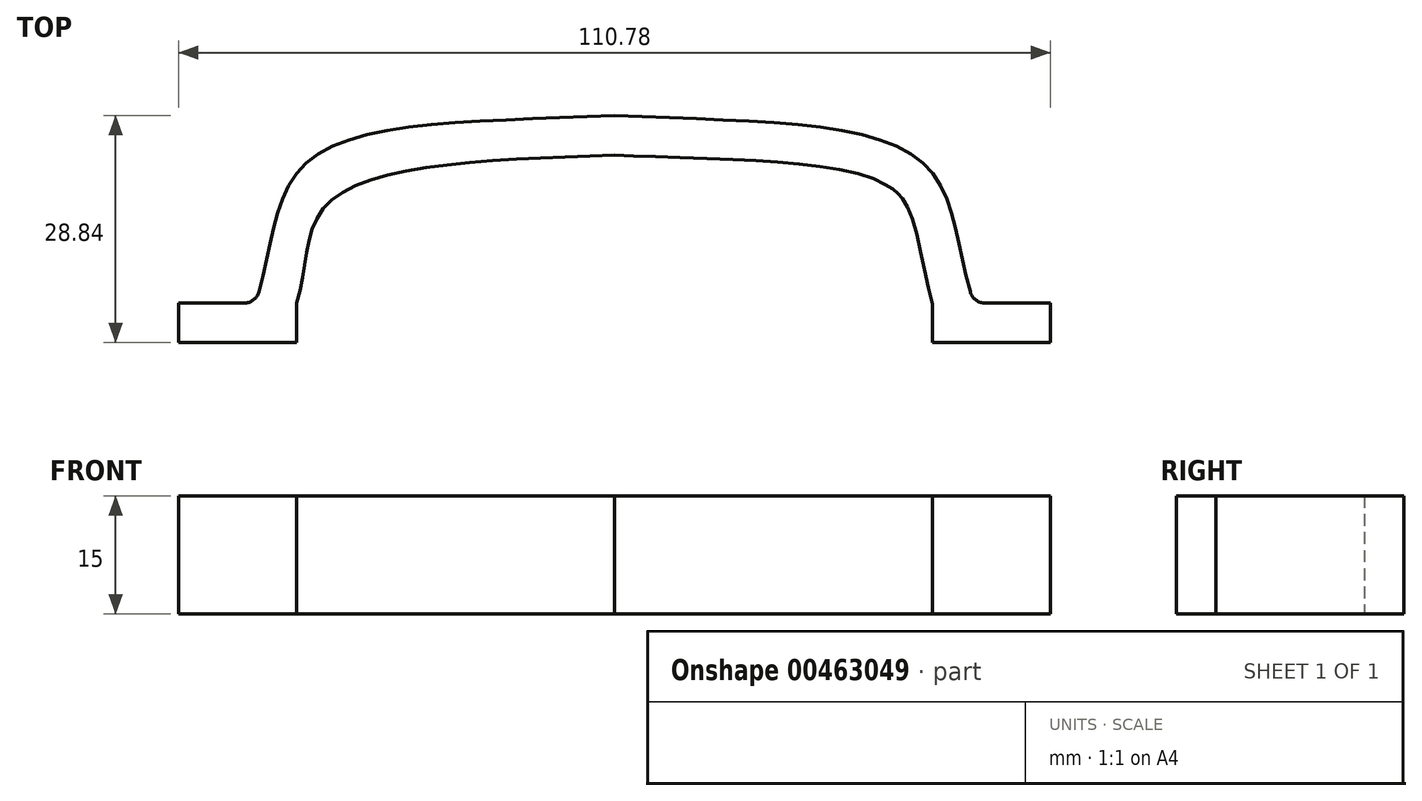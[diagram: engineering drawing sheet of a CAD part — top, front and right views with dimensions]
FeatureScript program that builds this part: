
annotation { "Feature Type Name" : "Feature", "Feature Type Description" : "" }
export const myFeature = defineFeature(function(context is Context, id is Id, definition is map)
    precondition{}
    {
        {
            var Q0;
            Q0=qCreatedBy(makeId("Top.planeOp"),FACE);
            var sketch = newSketch(context, id + "F0", { "sketchPlane" : qUnion([Q0])});
            skLineSegment(sketch, "E0.bottom", {"start": v(55.39, 0) * mm, "end": v(40.39, 0) * mm});
            skLineSegment(sketch, "E0.top", {"start": v(55.39, 5) * mm, "end": v(45.63, 5) * mm});
            skLineSegment(sketch, "E0.left", {"start": v(55.39, 0) * mm, "end": v(55.39, 5) * mm});
            skLineSegment(sketch, "E0.right", {"start": v(40.39, 0) * mm, "end": v(40.39, 5) * mm});
            skFitSpline(sketch, "E1", {"points": [v(45.63, 5) * mm, v(39.22, 22.75) * mm, v(0, 28.84) * mm], "startDerivative": vector(-16.27, 47.83) * mm, "endDerivative": vector(-83.04, 4.43) * mm});
            skFitSpline(sketch, "E2.0", {"points": [v(40.9, 3.39) * mm, v(40.5, 4.57) * mm, v(39.86, 6.87) * mm, v(39.17, 10.1) * mm, v(38.58, 12.98) * mm, v(37.94, 15.43) * mm, v(37.33, 17) * mm, v(36.79, 17.95) * mm, v(36.43, 18.45) * mm, v(36.13, 18.8) * mm, v(35.89, 19.03) * mm, v(35.62, 19.26) * mm, v(35.2, 19.58) * mm, v(34.55, 19.99) * mm, v(33.24, 20.63) * mm, v(31.1, 21.38) * mm, v(27.85, 22.09) * mm, v(24.02, 22.62) * mm, v(19.73, 22.99) * mm, v(15.07, 23.24) * mm, v(8.5, 23.49) * mm, v(3.26, 23.66) * mm, v(-0.27, 23.85) * mm]});
            skLineSegment(sketch, "E3.trimOffspring", {"start": v(40.39, 5) * mm, "end": v(40.39, 5) * mm});
            skLineSegment(sketch, "E4.MirrorCS", {"start": v(-40.39, 5) * mm, "end": v(-40.39, 5) * mm});
            skFitSpline(sketch, "E5.MirrorCS", {"points": [v(-45.63, 5) * mm, v(-39.22, 22.75) * mm, v(0, 28.84) * mm], "startDerivative": vector(16.27, 47.83) * mm, "endDerivative": vector(83.04, 4.43) * mm});
            skLineSegment(sketch, "E6.MirrorCS", {"start": v(-40.39, 0) * mm, "end": v(-40.39, 5) * mm});
            skLineSegment(sketch, "E7.MirrorCS", {"start": v(-55.39, 0) * mm, "end": v(-55.39, 5) * mm});
            skLineSegment(sketch, "E8.MirrorCS", {"start": v(-55.39, 0) * mm, "end": v(-40.39, 0) * mm});
            skLineSegment(sketch, "E9.MirrorCS", {"start": v(-55.39, 5) * mm, "end": v(-45.63, 5) * mm});
            skFitSpline(sketch, "E10", {"points": [v(-40.39, 5) * mm, v(-36.36, 17.71) * mm, v(0, 23.84) * mm], "startDerivative": vector(11.4, 37.26) * mm, "endDerivative": vector(71.64, 2.98) * mm});
            skSolve(sketch);
        }
        {
            var Q0;
            Q0=makeQuery(id+"F0.imprint","IMPRINT",FACE,{"disambiguationData":[TD([[makeQuery(id+"F0.imprint","IMPRINT",EDGE,{"derivedFrom":sQuery(id+"F0.wireOp",EDGE,"E0.bottom")}),-1.0]])]});
            extrude(context, id + "F1", {"entities" : qUnion([Q0]), "depth" : 15 * mm});
        }
        {
            var Q0;
            Q0=makeQuery(id+"F1.opExtrude","SWEPT_EDGE",EDGE,{"disambiguationData":[OSD([sQuery(id+"F0.wireOp",EDGE,"E5.MirrorCS"),sQuery(id+"F0.wireOp",EDGE,"E9.MirrorCS")])]});
            var Q1;
            Q1=makeQuery(id+"F1.opExtrude","SWEPT_EDGE",EDGE,{"disambiguationData":[OSD([sQuery(id+"F0.wireOp",EDGE,"E0.top"),sQuery(id+"F0.wireOp",EDGE,"E1")])]});
            fillet(context, id + "F2", {"entities" : qUnion([Q0, Q1]), "radius" : 2 * mm, "tangentPropagation" : true, "allowEdgeOverflow" : false});
        }
    });
